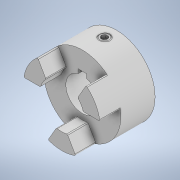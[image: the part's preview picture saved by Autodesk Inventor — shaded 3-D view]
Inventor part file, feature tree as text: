
AUTODESK INVENTOR PART (.ipt)
format: ipt  version: 2021 (Build 250183000, 183)  size: 185,856 bytes
history: native  units: in
note: dims shown in document units (in); Inventor stores cm internally (conversion verified against a paired STEP export)
features: other x1, chamfer x1
ambient origin geometry x8: Origin, YZ Plane, XZ Plane, XY Plane, X Axis, Y Axis, Z Axis, Center Point
bodies: Solid1 (feature_tree), Solid2 (feature_tree)
feature tree (2):
  other  "Cut-Extrude2"
  chamfer  "Chamfer4"  [1 undecoded]
note: 1 required parameter value undecoded (feature->parameter linkage not recoverable at this tier; creation-order binding heuristic only, values carry confidence <= 0.55)
